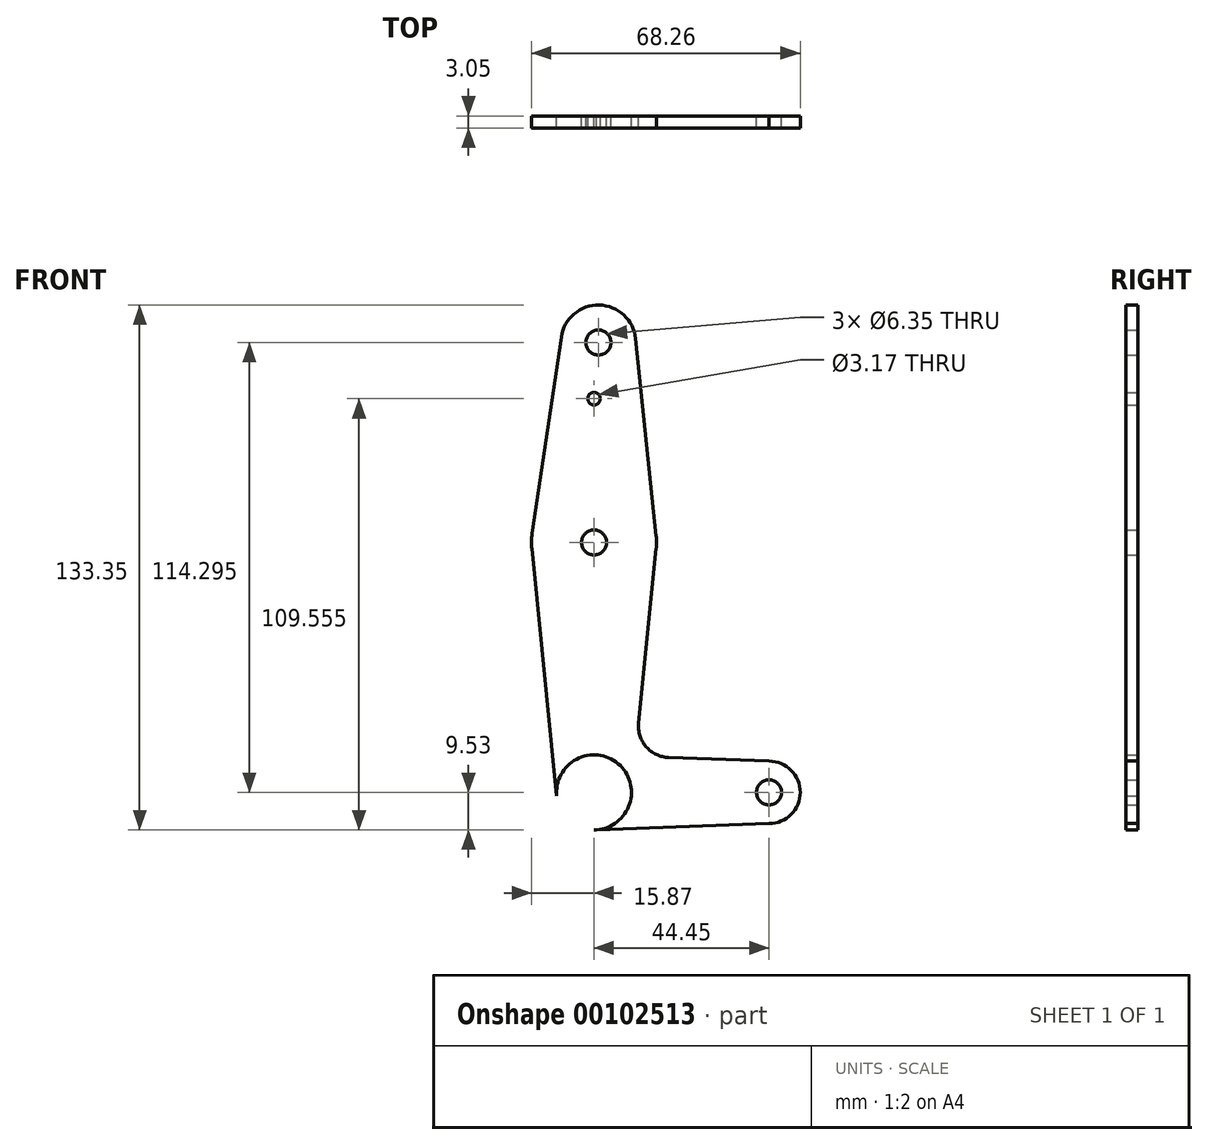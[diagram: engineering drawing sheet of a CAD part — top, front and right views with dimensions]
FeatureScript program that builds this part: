
annotation { "Feature Type Name" : "Feature", "Feature Type Description" : "" }
export const myFeature = defineFeature(function(context is Context, id is Id, definition is map)
    precondition{}
    {
        {
            var Q0;
            Q0=qCreatedBy(makeId("Front.planeOp"),FACE);
            var sketch = newSketch(context, id + "F0", { "sketchPlane" : qUnion([Q0])});
            skLineSegment(sketch, "E0", {"start": v(0, 0) * mm, "end": v(0, -42.68) * mm});
            skLineSegment(sketch, "E1", {"start": v(0, 0) * mm, "end": v(-44.13, 0) * mm});
            skLineSegment(sketch, "E2", {"start": v(0, 0) * mm, "end": v(44.45, 0) * mm});
            skCircle(sketch, "E3", {"center": v(0, 0) * mm, "radius": 9.53 * mm});
            skCircle(sketch, "E4", {"center": v(44.45, 0) * mm, "radius": 7.94 * mm});
            skCircle(sketch, "E5", {"center": v(1.1, 114.3) * mm, "radius": 9.53 * mm});
            skCircle(sketch, "E6", {"center": v(0, 63.5) * mm, "radius": 15.88 * mm});
            skLineSegment(sketch, "E7", {"start": v(-8.31, 115.7) * mm, "end": v(-15.7, 65.83) * mm});
            skLineSegment(sketch, "E8", {"start": v(10.58, 115.28) * mm, "end": v(15.8, 65.14) * mm});
            skLineSegment(sketch, "E9", {"start": v(44.45, -7.94) * mm, "end": v(0, -9.52) * mm});
            skLineSegment(sketch, "E10", {"start": v(44.45, 7.94) * mm, "end": v(18.97, 8.85) * mm});
            skLineSegment(sketch, "E11", {"start": v(-15.8, 61.91) * mm, "end": v(-9.48, -0.95) * mm});
            skLineSegment(sketch, "E12", {"start": v(15.8, 61.91) * mm, "end": v(11.34, 17.6) * mm});
            skPoint(sketch, "E13.newPointB", {"position": v(0, 9.53) * mm});
            skArc(sketch, "E13.filletArc", {"start": v(10.25, 6.79) * mm, "mid": v(14.45, 4.62) * mm, "end": v(12.87, 9.07) * mm});
            skArc(sketch, "E14.filletArc", {"start": v(11.34, 17.6) * mm, "mid": v(13.26, 11.57) * mm, "end": v(18.97, 8.85) * mm});
            skCircle(sketch, "E15", {"center": v(0, 100.03) * mm, "radius": 1.59 * mm});
            skCircle(sketch, "E16", {"center": v(1.1, 114.3) * mm, "radius": 3.18 * mm});
            skCircle(sketch, "E17", {"center": v(0, 0) * mm, "radius": 3.18 * mm});
            skCircle(sketch, "E18", {"center": v(44.45, 0) * mm, "radius": 3.18 * mm});
            skCircle(sketch, "E19", {"center": v(0, 63.5) * mm, "radius": 3.18 * mm});
            skSolve(sketch);
        }
        {
            var Q0;
            {var subQ0=sQuery(id+"F0.wireOp",EDGE,"E9");var subQ1=sQuery(id+"F0.wireOp",EDGE,"E3");var subQ3=makeQuery(id+"F0.imprint","INTERSECT",VERTEX,{"derivedFrom":[subQ1,subQ0]});Q0=makeQuery(id+"F0.imprint","IMPRINT",FACE,{"disambiguationData":[TD([[makeQuery(id+"F0.imprint","IMPRINT",EDGE,{"disambiguationData":[TD([[subQ3,1.0]])],"derivedFrom":subQ1}),1.0]])]});}
            var Q1;
            {var subQ0=sQuery(id+"F0.wireOp",EDGE,"E11");var subQ1=sQuery(id+"F0.wireOp",EDGE,"E1");var subQ2=makeQuery(id+"F0.imprint","INTERSECT",VERTEX,{"derivedFrom":[subQ1,subQ0]});Q1=makeQuery(id+"F0.imprint","IMPRINT",FACE,{"disambiguationData":[TD([[makeQuery(id+"F0.imprint","IMPRINT",EDGE,{"disambiguationData":[TD([[subQ2,1.0]])],"derivedFrom":subQ1}),1.0]])]});}
            var Q2;
            Q2=makeQuery(id+"F0.imprint","IMPRINT",FACE,{"disambiguationData":[TD([[makeQuery(id+"F0.imprint","IMPRINT",EDGE,{"derivedFrom":sQuery(id+"F0.wireOp",EDGE,"E16")}),-1.0]])]});
            var Q3;
            {var subQ0=sQuery(id+"F0.wireOp",EDGE,"E4");var subQ1=sQuery(id+"F0.wireOp",EDGE,"E2");var subQ2=makeQuery(id+"F0.imprint","INTERSECT",VERTEX,{"derivedFrom":[subQ1,subQ0]});Q3=makeQuery(id+"F0.imprint","IMPRINT",FACE,{"disambiguationData":[TD([[makeQuery(id+"F0.imprint","IMPRINT",EDGE,{"disambiguationData":[TD([[subQ2,1.0]])],"derivedFrom":subQ1}),-1.0]])]});}
            var Q4;
            Q4=makeQuery(id+"F0.imprint","IMPRINT",FACE,{"disambiguationData":[TD([[makeQuery(id+"F0.imprint","IMPRINT",EDGE,{"derivedFrom":sQuery(id+"F0.wireOp",EDGE,"E18")}),-1.0]])]});
            var Q5;
            {var subQ0=sQuery(id+"F0.wireOp",EDGE,"E7");Q5=makeQuery(id+"F0.imprint","IMPRINT",FACE,{"disambiguationData":[TD([[makeQuery(id+"F0.imprint","IMPRINT",EDGE,{"derivedFrom":subQ0}),1.0]])]});}
            var Q6;
            Q6=makeQuery(id+"F0.imprint","IMPRINT",FACE,{"disambiguationData":[TD([[makeQuery(id+"F0.imprint","IMPRINT",EDGE,{"derivedFrom":sQuery(id+"F0.wireOp",EDGE,"E19")}),-1.0]])]});
            var Q7;
            {var subQ0=sQuery(id+"F0.wireOp",EDGE,"E10");Q7=makeQuery(id+"F0.imprint","IMPRINT",FACE,{"disambiguationData":[TD([[makeQuery(id+"F0.imprint","IMPRINT",EDGE,{"derivedFrom":subQ0}),1.0]])]});}
            extrude(context, id + "F1", {"entities" : qUnion([Q0, Q1, Q2, Q3, Q4, Q5, Q6, Q7]), "depth" : 3.05 * mm});
        }
    });
